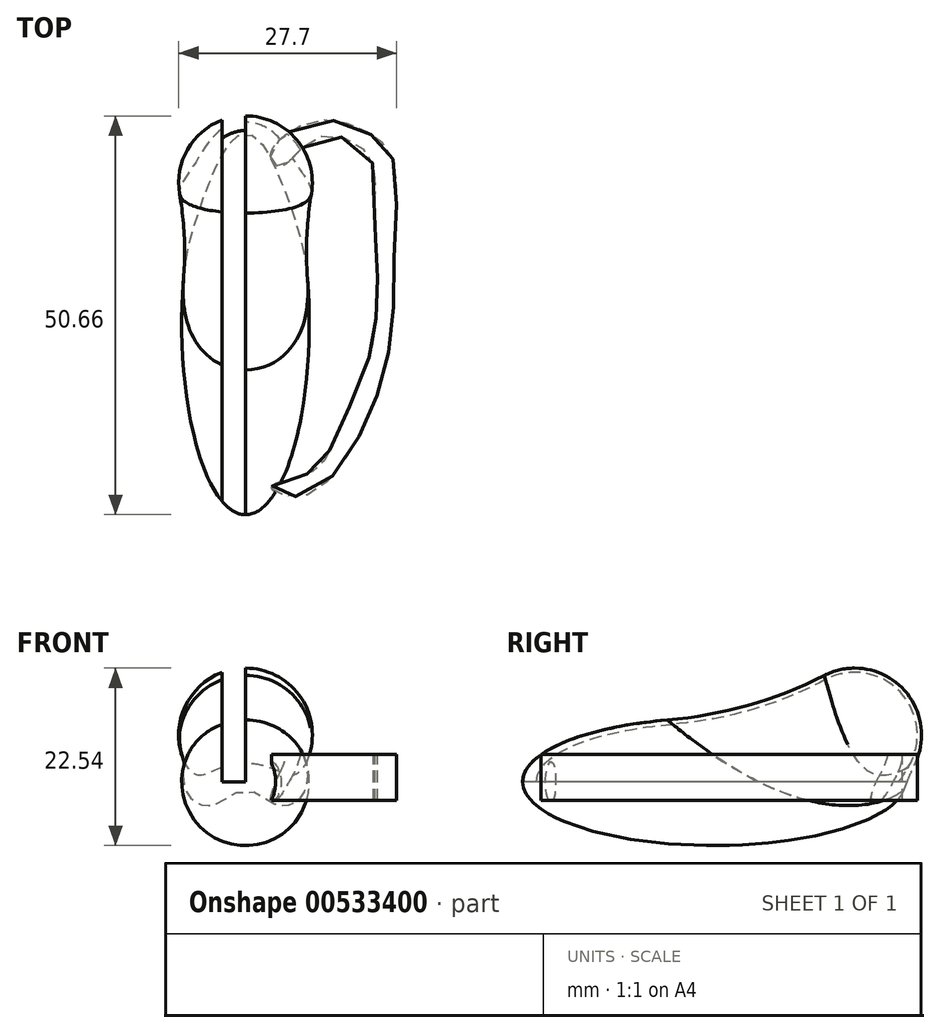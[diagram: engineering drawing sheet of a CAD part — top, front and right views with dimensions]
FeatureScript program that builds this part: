
annotation { "Feature Type Name" : "Feature", "Feature Type Description" : "" }
export const myFeature = defineFeature(function(context is Context, id is Id, definition is map)
    precondition{}
    {
        {
            var Q0;
            Q0=qCreatedBy(makeId("Top.planeOp"),FACE);
            var sketch = newSketch(context, id + "F0", { "sketchPlane" : qUnion([Q0])});
            skEllipse(sketch, "E0", {"center": v(0, 0) * mm, "majorRadius": 45 * mm, "minorRadius": 15 * mm, "majorAxis": v(0, -1)});
            skLineSegment(sketch, "E1", {"start": v(0, 45) * mm, "end": v(0, -45) * mm});
            skSolve(sketch);
        }
        {
            var Q0;
            Q0=makeQuery(id+"F0.imprint","IMPRINT",FACE,{"disambiguationData":[TD([[makeQuery(id+"F0.imprint","IMPRINT",EDGE,{"derivedFrom":sQuery(id+"F0.wireOp",EDGE,"E0")}),1.0]])]});
            var sketch = newSketch(context, id + "F1", { "sketchPlane" : qUnion([Q0])});
            skSolve(sketch);
        }
        {
            var Q0;
            Q0=makeQuery(id+"F1.imprint","IMPRINT",FACE,{"disambiguationData":[TD([[makeQuery(id+"F1.imprint","IMPRINT",EDGE,{"derivedFrom":makeQuery(id+"F0.imprint","IMPRINT",EDGE,{"derivedFrom":sQuery(id+"F0.wireOp",EDGE,"E0")})}),1.0]])]});
            var sketch = newSketch(context, id + "F2", { "sketchPlane" : qUnion([Q0])});
            skLineSegment(sketch, "E2", {"start": v(0, 44.96) * mm, "end": v(0, -45.26) * mm});
            skSolve(sketch);
        }
        {
            var Q0;
            {var subQ0=sQuery(id+"F0.wireOp",EDGE,"E1");Q0=makeQuery(id+"F0.imprint","IMPRINT",FACE,{"disambiguationData":[TD([[makeQuery(id+"F0.imprint","IMPRINT",EDGE,{"derivedFrom":subQ0}),-1.0]])]});}
            var Q1;
            Q1=sQuery(id+"F2.wireOp",EDGE,"E2");
            revolve(context, id + "F3", {"entities" : qUnion([Q0]), "axis" : qUnion([Q1]), "revolveType" : RevolveType.FULL});
        }
        {
            var Q0;
            Q0=qCreatedBy(makeId("Right.planeOp"),FACE);
            var sketch = newSketch(context, id + "F4", { "sketchPlane" : qUnion([Q0])});
            skCircle(sketch, "E3", {"center": v(33.1, 11.03) * mm, "radius": 15.72 * mm});
            skLineSegment(sketch, "E4", {"start": v(33.1, 11.03) * mm, "end": v(33.1, 26.75) * mm});
            skLineSegment(sketch, "E5", {"start": v(33.1, 26.75) * mm, "end": v(33.1, -4.7) * mm});
            skSolve(sketch);
        }
        {
            var Q0;
            {var subQ0=sQuery(id+"F4.wireOp",EDGE,"E5");var subQ4=makeQuery(id+"F4.imprint","IMPRINT",VERTEX,{"derivedFrom":subQ0});Q0=makeQuery(id+"F4.imprint","IMPRINT",FACE,{"disambiguationData":[TD([[makeQuery(id+"F4.imprint","IMPRINT",EDGE,{"disambiguationData":[TD([[subQ4,1.0]])],"derivedFrom":subQ0}),1.0]])]});}
            var Q1;
            Q1=sQuery(id+"F4.wireOp",EDGE,"E5");
            revolve(context, id + "F5", {"operationType" : NewBodyOperationType.ADD, "entities" : qUnion([Q0]), "axis" : qUnion([Q1]), "revolveType" : RevolveType.FULL});
        }
        {
            var Q0;
            Q0=makeQuery(id+"F5.boolean.opBoolean","INTERSECT",EDGE,{"derivedFrom":[makeQuery(id+"F3.opRevolve","SWEPT_FACE",FACE,{"disambiguationData":[OSD([sQuery(id+"F0.wireOp",EDGE,"E0")])]}),makeQuery(id+"F5.opRevolve","SWEPT_FACE",FACE,{"disambiguationData":[OSD([sQuery(id+"F4.wireOp",EDGE,"E3")])]})]});
            fillet(context, id + "F6", {"entities" : qUnion([Q0]), "radius" : 100 * mm, "tangentPropagation" : true, "allowEdgeOverflow" : false});
        }
        {
            var Q0;
            Q0=qCreatedBy(makeId("Top.planeOp"),FACE);
            cPlane(context, id + "F7", {"entities" : qUnion([Q0]), "cplaneType" : CPlaneType.OFFSET, "offset" : 15 * mm, "oppositeDirection" : true, "width" : 150 * mm, "height" : 150 * mm});
        }
        {
            var Q0;
            Q0=qCreatedBy(makeId("Top.planeOp"),FACE);
            cPlane(context, id + "F8", {"entities" : qUnion([Q0]), "cplaneType" : CPlaneType.OFFSET, "offset" : 6 * mm, "oppositeDirection" : true, "width" : 150 * mm, "height" : 150 * mm});
        }
        {
            var Q0;
            Q0=qCreatedBy(makeId("Right.planeOp"),FACE);
            var sketch = newSketch(context, id + "F9", { "sketchPlane" : qUnion([Q0])});
            skLineSegment(sketch, "E6.bottom", {"start": v(55.32, 38.46) * mm, "end": v(-65.17, 38.46) * mm});
            skLineSegment(sketch, "E6.top", {"start": v(55.32, 0) * mm, "end": v(-65.17, 0) * mm});
            skLineSegment(sketch, "E6.left", {"start": v(55.32, 38.46) * mm, "end": v(55.32, 0) * mm});
            skLineSegment(sketch, "E6.right", {"start": v(-65.17, 38.46) * mm, "end": v(-65.17, 0) * mm});
            skSolve(sketch);
        }
        {
            var Q0;
            Q0=qSketchRegion(id+"F9",true);
            extrude(context, id + "F10", {"entities" : qUnion([Q0]), "operationType" : NewBodyOperationType.REMOVE, "oppositeDirection" : true, "depth" : 5.54 * mm, "offsetDistance" : 25 * mm});
        }
        {
            var Q0;
            Q0=qCreatedBy(id+"F8.planeOp",FACE);
            cPlane(context, id + "F11", {"entities" : qUnion([Q0]), "cplaneType" : CPlaneType.OFFSET, "offset" : 1.6 * mm, "width" : 150 * mm, "height" : 150 * mm});
        }
        {
            var Q0;
            Q0=qCreatedBy(id+"F11.planeOp",FACE);
            var sketch = newSketch(context, id + "F12", { "sketchPlane" : qUnion([Q0])});
            skFitSpline(sketch, "E7", {"points": [v(8.31, 36.97) * mm, v(16.84, 43.75) * mm, v(29.1, 39.38) * mm, v(30.19, 27.78) * mm, v(30.84, 17.28) * mm, v(30.84, 3.72) * mm, v(28.88, -8.53) * mm, v(20.56, -28.22) * mm, v(15.1, -35.22) * mm, v(6.13, -38.5) * mm, v(12.69, -40.69) * mm, v(24.5, -30.4) * mm, v(31.28, -15.75) * mm, v(34.56, 0) * mm, v(35, 19.03) * mm, v(34.78, 38.28) * mm, v(28.88, 44.84) * mm, v(15.97, 47.47) * mm, v(5.9, 39.6) * mm, v(8.31, 36.97) * mm]});
            skSolve(sketch);
        }
        {
            var Q0;
            Q0 = qSketchRegion(id + "F12", true);
            extrude(context, id + "F13", {"entities" : qUnion([Q0]), "operationType" : NewBodyOperationType.ADD, "depth" : 10.9 * mm, "offsetDistance" : 25 * mm});
        }
        {
            var Q0;
            Q0=makeQuery(id+"F3.opRevolve","SWEPT_BODY",BODY,{"disambiguationData":[OSD([sQuery(id+"F0.wireOp",EDGE,"E0"),sQuery(id+"F0.wireOp",EDGE,"E1")])]});
            var Q1;
            Q1=qCreatedBy(makeId("Origin.pointOp"),VERTEX);
            transform(context, id + "F14", {"entities" : qUnion([Q0]), "transformType" : TransformType.SCALE_UNIFORMLY, "scale" : .54, "scalePoint" : qUnion([Q1]), "makeCopy" : false});
        }
    });
